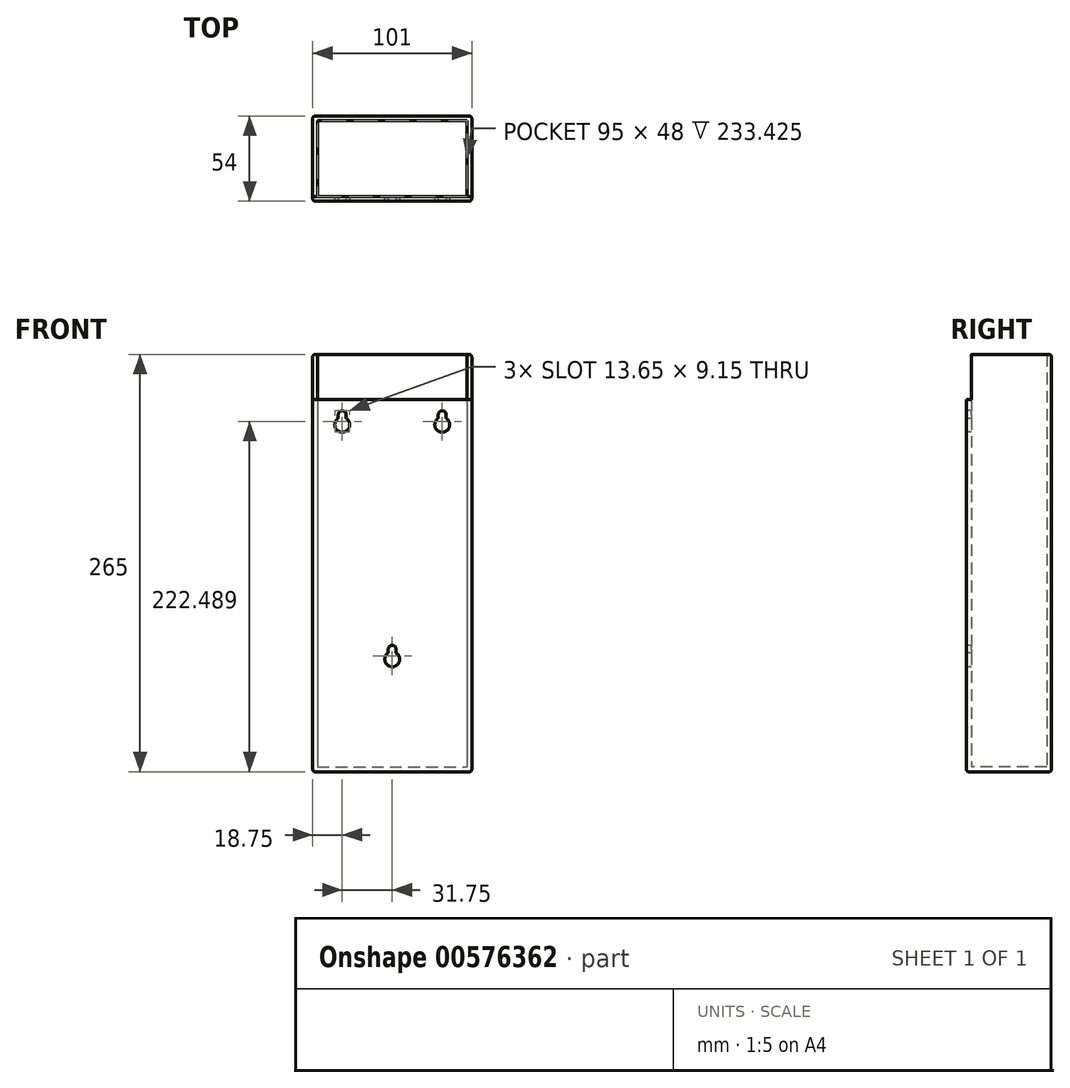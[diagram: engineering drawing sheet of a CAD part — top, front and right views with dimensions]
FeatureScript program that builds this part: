
annotation { "Feature Type Name" : "Feature", "Feature Type Description" : "" }
export const myFeature = defineFeature(function(context is Context, id is Id, definition is map)
    precondition{}
    {
        {
            var Q0;
            Q0=qCreatedBy(makeId("Top.planeOp"),FACE);
            var sketch = newSketch(context, id + "F0", { "sketchPlane" : qUnion([Q0])});
            skLineSegment(sketch, "E0", {"start": v(0, 32.2) * mm, "end": v(0, -33) * mm, "construction": true});
            skLineSegment(sketch, "E1", {"start": v(-55.74, 0) * mm, "end": v(56.26, 0) * mm, "construction": true});
            skLineSegment(sketch, "E2.bottom", {"start": v(-50.5, 27) * mm, "end": v(50.5, 27) * mm});
            skLineSegment(sketch, "E2.top", {"start": v(-50.5, -27) * mm, "end": v(50.5, -27) * mm});
            skLineSegment(sketch, "E2.left", {"start": v(-50.5, 27) * mm, "end": v(-50.5, -27) * mm});
            skLineSegment(sketch, "E2.right", {"start": v(50.5, 27) * mm, "end": v(50.5, -27) * mm});
            skSolve(sketch);
        }
        {
            var Q0;
            Q0 = qSketchRegion(id + "F0", true);
            extrude(context, id + "F1", {"entities" : qUnion([Q0]), "depth" : 265 * mm, "offsetDistance" : 25 * mm, "symmetric" : true});
        }
        {
            var Q0;
            Q0=makeQuery(id+"F1.opExtrude","CAP_FACE",FACE,{"disambiguationData":[OSD([sQuery(id+"F0.wireOp",EDGE,"E2.bottom"),sQuery(id+"F0.wireOp",EDGE,"E2.top"),sQuery(id+"F0.wireOp",EDGE,"E2.left"),sQuery(id+"F0.wireOp",EDGE,"E2.right")])],"isStart":false});
            shell(context, id + "F2", {"entities" : qUnion([Q0]), "thickness" : 3 * mm});
        }
        {
            var Q0;
            Q0=makeQuery(id+"F1.opExtrude","SWEPT_FACE",FACE,{"disambiguationData":[OSD([sQuery(id+"F0.wireOp",EDGE,"E2.top")])]});
            var sketch = newSketch(context, id + "F3", { "sketchPlane" : qUnion([Q0])});
            skLineSegment(sketch, "E3", {"start": v(-50.5, 103.92) * mm, "end": v(50.5, 103.92) * mm});
            skLineSegment(sketch, "E4", {"start": v(50.5, 103.92) * mm, "end": v(50.5, 132.5) * mm});
            skLineSegment(sketch, "E5", {"start": v(50.5, 132.5) * mm, "end": v(-50.5, 132.5) * mm});
            skLineSegment(sketch, "E6", {"start": v(-50.5, 132.5) * mm, "end": v(-50.5, 103.92) * mm});
            skSolve(sketch);
        }
        {
            var Q0;
            Q0 = qSketchRegion(id + "F3", true);
            var Q1;
            Q1=makeQuery(id+"F2.opShell","OFFSET_FACE",FACE,{"disambiguationData":[OSD([sQuery(id+"F0.wireOp",EDGE,"E2.top")])]});
            extrude(context, id + "F4", {"entities" : qUnion([Q0]), "operationType" : NewBodyOperationType.REMOVE, "endBound" : BoundingType.UP_TO_SURFACE, "oppositeDirection" : true, "depth" : 25 * mm, "endBoundEntityFace" : qUnion([Q1]), "offsetDistance" : 25 * mm});
        }
        {
            var Q0;
            Q0=makeQuery(id+"F1.opExtrude","SWEPT_FACE",FACE,{"disambiguationData":[OSD([sQuery(id+"F0.wireOp",EDGE,"E2.top")])]});
            var sketch = newSketch(context, id + "F5", { "sketchPlane" : qUnion([Q0])});
            skLineSegment(sketch, "E7", {"start": v(0, 233.66) * mm, "end": v(0, -9.7) * mm, "construction": true});
            skLineSegment(sketch, "E8", {"start": v(-43.12, 87.92) * mm, "end": v(39.63, 87.92) * mm, "construction": true});
            skArc(sketch, "E9", {"start": v(-34.29, 91.95) * mm, "mid": v(-31.75, 83.16) * mm, "end": v(-29.2, 91.95) * mm});
            skArc(sketch, "E10", {"start": v(-29.2, 94.27) * mm, "mid": v(-31.75, 96.81) * mm, "end": v(-34.29, 94.27) * mm});
            skLineSegment(sketch, "E11", {"start": v(-31.75, 233.66) * mm, "end": v(-31.75, 213.57) * mm, "construction": true});
            skLineSegment(sketch, "E12", {"start": v(-34.29, 94.27) * mm, "end": v(-34.29, 91.95) * mm});
            skLineSegment(sketch, "E13", {"start": v(-29.2, 94.27) * mm, "end": v(-29.2, 91.95) * mm});
            skLineSegment(sketch, "E14.MirrorCS", {"start": v(31.75, 233.66) * mm, "end": v(31.75, 213.57) * mm, "construction": true});
            skArc(sketch, "E15.MirrorCS", {"start": v(29.2, 94.27) * mm, "mid": v(31.75, 96.81) * mm, "end": v(34.29, 94.27) * mm});
            skLineSegment(sketch, "E16.MirrorCS", {"start": v(34.3, 94.27) * mm, "end": v(34.3, 91.95) * mm});
            skArc(sketch, "E17.MirrorCS", {"start": v(34.29, 91.95) * mm, "mid": v(31.75, 83.16) * mm, "end": v(29.2, 91.95) * mm});
            skLineSegment(sketch, "E18.MirrorCS", {"start": v(29.21, 94.27) * mm, "end": v(29.21, 91.95) * mm});
            skArc(sketch, "E19", {"start": v(-2.54, -57.05) * mm, "mid": v(0, -65.84) * mm, "end": v(2.54, -57.05) * mm});
            skArc(sketch, "E20", {"start": v(2.54, -54.73) * mm, "mid": v(0, -52.19) * mm, "end": v(-2.54, -54.73) * mm});
            skLineSegment(sketch, "E21", {"start": v(-2.54, -54.73) * mm, "end": v(-2.54, -57.05) * mm});
            skLineSegment(sketch, "E22", {"start": v(2.54, -54.73) * mm, "end": v(2.54, -57.05) * mm});
            skLineSegment(sketch, "E23", {"start": v(-13.54, -61.08) * mm, "end": v(9.91, -61.08) * mm, "construction": true});
            skSolve(sketch);
        }
        {
            var Q0;
            Q0 = qSketchRegion(id + "F5", true);
            var Q1;
            Q1=makeQuery(id+"F2.opShell","OFFSET_FACE",FACE,{"disambiguationData":[OSD([sQuery(id+"F0.wireOp",EDGE,"E2.top")])]});
            extrude(context, id + "F6", {"entities" : qUnion([Q0]), "operationType" : NewBodyOperationType.REMOVE, "endBound" : BoundingType.UP_TO_SURFACE, "oppositeDirection" : true, "depth" : 25 * mm, "endBoundEntityFace" : qUnion([Q1]), "offsetDistance" : 25 * mm});
        }
        {
            var Q0;
            Q0=makeQuery(id+"F1.opExtrude","SWEPT_EDGE",EDGE,{"disambiguationData":[OSD([sQuery(id+"F0.wireOp",EDGE,"E2.top"),sQuery(id+"F0.wireOp",EDGE,"E2.right")])]});
            var Q1;
            Q1=makeQuery(id+"F1.opExtrude","SWEPT_EDGE",EDGE,{"disambiguationData":[OSD([sQuery(id+"F0.wireOp",EDGE,"E2.bottom"),sQuery(id+"F0.wireOp",EDGE,"E2.right")])]});
            var Q2;
            Q2=makeQuery(id+"F1.opExtrude","SWEPT_EDGE",EDGE,{"disambiguationData":[OSD([sQuery(id+"F0.wireOp",EDGE,"E2.top"),sQuery(id+"F0.wireOp",EDGE,"E2.left")])]});
            var Q3;
            Q3=makeQuery(id+"F1.opExtrude","SWEPT_EDGE",EDGE,{"disambiguationData":[OSD([sQuery(id+"F0.wireOp",EDGE,"E2.bottom"),sQuery(id+"F0.wireOp",EDGE,"E2.left")])]});
            var Q4;
            Q4=makeQuery(id+"F1.opExtrude","CAP_EDGE",EDGE,{"disambiguationData":[OSD([sQuery(id+"F0.wireOp",EDGE,"E2.left")])],"isStart":true});
            var Q5;
            Q5=makeQuery(id+"F1.opExtrude","CAP_EDGE",EDGE,{"disambiguationData":[OSD([sQuery(id+"F0.wireOp",EDGE,"E2.bottom")])],"isStart":true});
            var Q6;
            Q6=makeQuery(id+"F1.opExtrude","CAP_EDGE",EDGE,{"disambiguationData":[OSD([sQuery(id+"F0.wireOp",EDGE,"E2.top")])],"isStart":true});
            var Q7;
            Q7=makeQuery(id+"F1.opExtrude","CAP_EDGE",EDGE,{"disambiguationData":[OSD([sQuery(id+"F0.wireOp",EDGE,"E2.right")])],"isStart":true});
            var Q8;
            Q8=makeQuery(id+"F1.opExtrude","CAP_EDGE",EDGE,{"disambiguationData":[OSD([sQuery(id+"F0.wireOp",EDGE,"E2.left")])],"isStart":false});
            var Q9;
            Q9=makeQuery(id+"F1.opExtrude","CAP_EDGE",EDGE,{"disambiguationData":[OSD([sQuery(id+"F0.wireOp",EDGE,"E2.bottom")])],"isStart":false});
            var Q10;
            Q10=makeQuery(id+"F1.opExtrude","CAP_EDGE",EDGE,{"disambiguationData":[OSD([sQuery(id+"F0.wireOp",EDGE,"E2.right")])],"isStart":false});
            var Q11;
            Q11=makeQuery(id+"F4.boolean.opBoolean","COPY",EDGE,{"derivedFrom":makeQuery(id+"F4.opExtrude","CAP_EDGE",EDGE,{"disambiguationData":[OSD([sQuery(id+"F3.wireOp",EDGE,"E3")])],"isStart":true})});
            var Q12;
            Q12=makeQuery(id+"F4.boolean.opBoolean","COPY",EDGE,{"derivedFrom":makeQuery(id+"F4.opExtrude","TWEAK_EDGE",EDGE,{"derivedFrom":[makeQuery(id+"F2.opShell","OFFSET_FACE",FACE,{"disambiguationData":[OSD([sQuery(id+"F0.wireOp",EDGE,"E2.top")])]}),makeQuery(id+"F3.imprint","IMPRINT",EDGE,{"derivedFrom":sQuery(id+"F3.wireOp",EDGE,"E6")})]})});
            var Q13;
            Q13=makeQuery(id+"F4.boolean.opBoolean","COPY",EDGE,{"derivedFrom":makeQuery(id+"F4.opExtrude","TWEAK_EDGE",EDGE,{"derivedFrom":[makeQuery(id+"F2.opShell","OFFSET_FACE",FACE,{"disambiguationData":[OSD([sQuery(id+"F0.wireOp",EDGE,"E2.top")])]}),makeQuery(id+"F3.imprint","IMPRINT",EDGE,{"derivedFrom":sQuery(id+"F3.wireOp",EDGE,"E4")})]})});
            fillet(context, id + "F7", {"entities" : qUnion([Q0, Q1, Q2, Q3, Q4, Q5, Q6, Q7, Q8, Q9, Q10, Q11, Q12, Q13]), "radius" : 1.5 * mm, "tangentPropagation" : true, "allowEdgeOverflow" : false});
        }
    });
